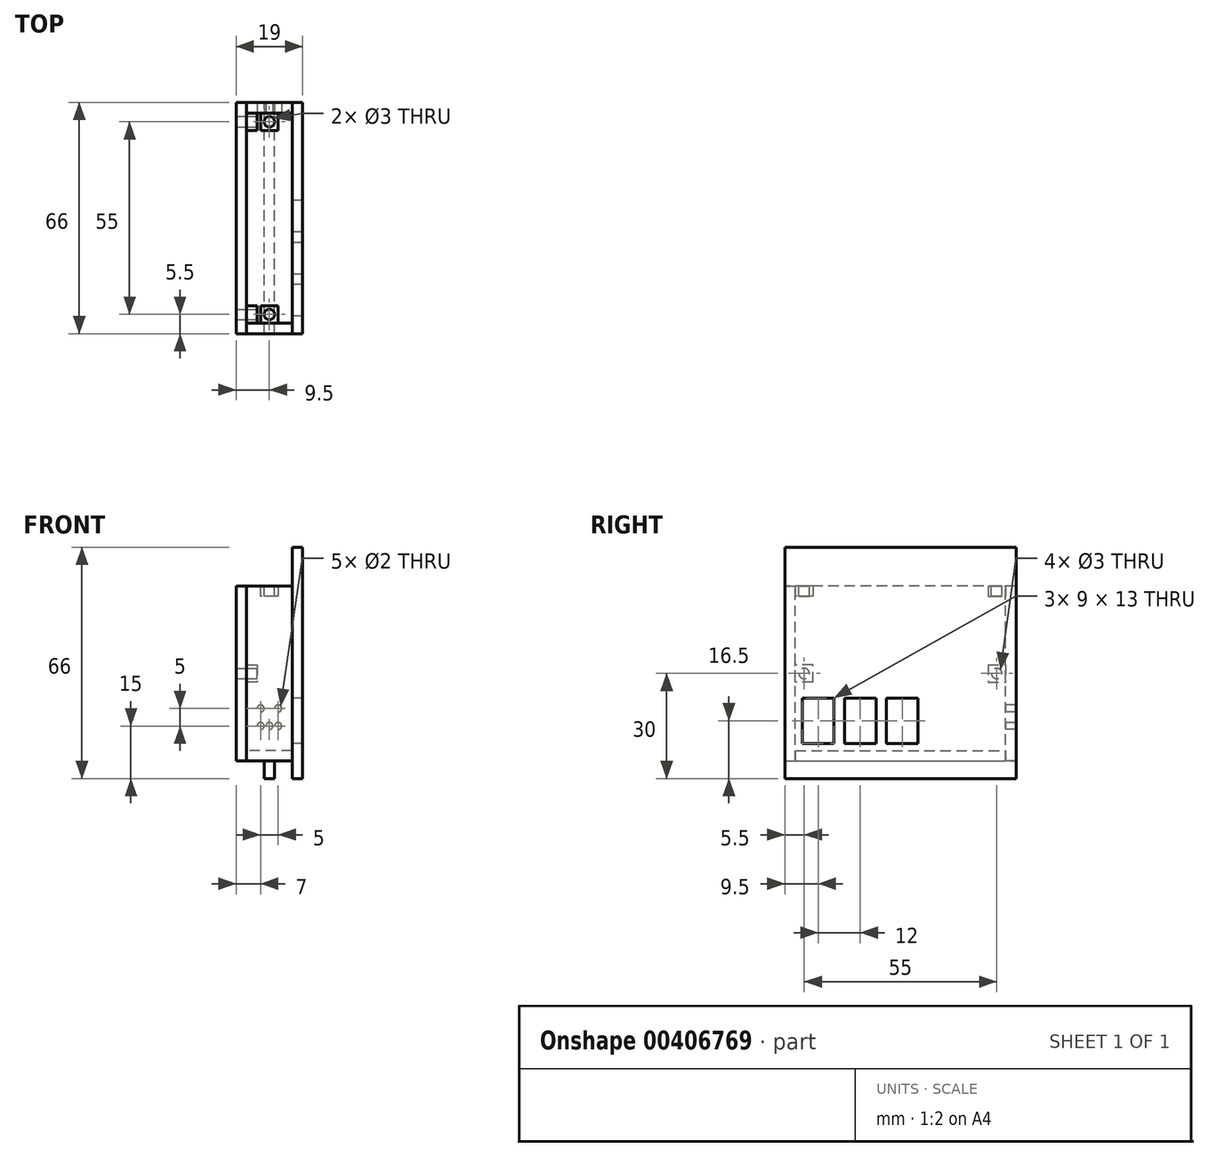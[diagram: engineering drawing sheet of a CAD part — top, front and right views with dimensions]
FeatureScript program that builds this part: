
annotation { "Feature Type Name" : "Feature", "Feature Type Description" : "" }
export const myFeature = defineFeature(function(context is Context, id is Id, definition is map)
    precondition{}
    {
        {
            var Q0;
            Q0=qCreatedBy(makeId("Top.planeOp"),FACE);
            var sketch = newSketch(context, id + "F0", { "sketchPlane" : qUnion([Q0])});
            skLineSegment(sketch, "E0.bottom", {"start": v(6.5, -30) * mm, "end": v(-6.5, -30) * mm});
            skLineSegment(sketch, "E0.top", {"start": v(6.5, 30) * mm, "end": v(-6.5, 30) * mm});
            skLineSegment(sketch, "E0.left", {"start": v(6.5, -30) * mm, "end": v(6.5, 30) * mm});
            skLineSegment(sketch, "E0.right", {"start": v(-6.5, -30) * mm, "end": v(-6.5, 30) * mm});
            skPoint(sketch, "E0.middle", {"position": v(0, 0) * mm});
            skSolve(sketch);
        }
        {
            var Q0;
            Q0=makeQuery(id+"F0.imprint","IMPRINT",FACE,{"disambiguationData":[TD([[makeQuery(id+"F0.imprint","IMPRINT",EDGE,{"derivedFrom":sQuery(id+"F0.wireOp",EDGE,"E0.bottom")}),-1.0]])]});
            extrude(context, id + "F1", {"entities" : qUnion([Q0]), "depth" : 3 * mm});
        }
        {
            var Q0;
            Q0=makeQuery(id+"F1.opExtrude","SWEPT_FACE",FACE,{"disambiguationData":[OSD([sQuery(id+"F0.wireOp",EDGE,"E0.top")])]});
            var sketch = newSketch(context, id + "F2", { "sketchPlane" : qUnion([Q0])});
            skLineSegment(sketch, "E1", {"start": v(-6.5, 0) * mm, "end": v(-6.5, 50) * mm});
            skLineSegment(sketch, "E2", {"start": v(-6.5, 50) * mm, "end": v(6.5, 50) * mm});
            skLineSegment(sketch, "E3", {"start": v(6.5, 50) * mm, "end": v(6.5, 0) * mm});
            skLineSegment(sketch, "E4", {"start": v(-6.5, 10) * mm, "end": v(6.5, 10) * mm, "construction": true});
            skLineSegment(sketch, "E5", {"start": v(-6.5, 12.5) * mm, "end": v(6.5, 12.5) * mm, "construction": true});
            skLineSegment(sketch, "E6", {"start": v(-6.5, 15) * mm, "end": v(6.5, 15) * mm, "construction": true});
            skLineSegment(sketch, "E7", {"start": v(0, 15) * mm, "end": v(0, 10) * mm, "construction": true});
            skLineSegment(sketch, "E8", {"start": v(2.5, 15) * mm, "end": v(2.5, 10) * mm, "construction": true});
            skLineSegment(sketch, "E9", {"start": v(-2.5, 15) * mm, "end": v(-2.5, 10) * mm, "construction": true});
            skCircle(sketch, "E10", {"center": v(-2.5, 15) * mm, "radius": 1 * mm});
            skCircle(sketch, "E11", {"center": v(2.5, 15) * mm, "radius": 1 * mm});
            skCircle(sketch, "E12", {"center": v(2.5, 10) * mm, "radius": 1 * mm});
            skCircle(sketch, "E13", {"center": v(0, 10) * mm, "radius": 1 * mm});
            skCircle(sketch, "E14", {"center": v(-2.5, 10) * mm, "radius": 1 * mm});
            skSolve(sketch);
        }
        {
            var Q0;
            {var subQ2=sQuery(id+"F2.wireOp",EDGE,"E2");Q0=makeQuery(id+"F2.imprint","IMPRINT",FACE,{"disambiguationData":[TD([[makeQuery(id+"F2.imprint","IMPRINT",EDGE,{"derivedFrom":subQ2}),-1.0]])]});}
            var Q1;
            {var subQ1=sQuery(id+"F0.wireOp",EDGE,"E0.top");var subQ2=makeQuery(id+"F1.opExtrude","CAP_EDGE",EDGE,{"disambiguationData":[OSD([subQ1])],"isStart":true});Q1=makeQuery(id+"F2.imprint","IMPRINT",FACE,{"disambiguationData":[TD([[makeQuery(id+"F2.imprint","IMPRINT",EDGE,{"derivedFrom":subQ2}),1.0]])]});}
            extrude(context, id + "F3", {"entities" : qUnion([Q0, Q1]), "depth" : 3 * mm});
        }
        {
            var Q0;
            Q0=makeQuery(id+"F1.opExtrude","SWEPT_FACE",FACE,{"disambiguationData":[OSD([sQuery(id+"F0.wireOp",EDGE,"E0.bottom")])]});
            var sketch = newSketch(context, id + "F4", { "sketchPlane" : qUnion([Q0])});
            skLineSegment(sketch, "E15", {"start": v(-6.5, 0) * mm, "end": v(-6.5, 50) * mm});
            skLineSegment(sketch, "E16", {"start": v(-6.5, 50) * mm, "end": v(6.5, 50) * mm});
            skLineSegment(sketch, "E17", {"start": v(6.5, 50) * mm, "end": v(6.5, 0) * mm});
            skSolve(sketch);
        }
        {
            var Q0;
            {var subQ2=sQuery(id+"F4.wireOp",EDGE,"E16");Q0=makeQuery(id+"F4.imprint","IMPRINT",FACE,{"disambiguationData":[TD([[makeQuery(id+"F4.imprint","IMPRINT",EDGE,{"derivedFrom":subQ2}),-1.0]])]});}
            var Q1;
            {var subQ1=sQuery(id+"F0.wireOp",EDGE,"E0.bottom");var subQ2=makeQuery(id+"F1.opExtrude","CAP_EDGE",EDGE,{"disambiguationData":[OSD([subQ1])],"isStart":true});Q1=makeQuery(id+"F4.imprint","IMPRINT",FACE,{"disambiguationData":[TD([[makeQuery(id+"F4.imprint","IMPRINT",EDGE,{"derivedFrom":subQ2}),-1.0]])]});}
            extrude(context, id + "F5", {"entities" : qUnion([Q0, Q1]), "depth" : 3 * mm});
        }
        {
            var Q0;
            Q0=makeQuery(id+"F1.opExtrude","SWEPT_FACE",FACE,{"disambiguationData":[OSD([sQuery(id+"F0.wireOp",EDGE,"E0.left")])]});
            var sketch = newSketch(context, id + "F6", { "sketchPlane" : qUnion([Q0])});
            skLineSegment(sketch, "E18.bottom", {"start": v(-33, 61) * mm, "end": v(33, 61) * mm});
            skLineSegment(sketch, "E18.top", {"start": v(-33, -5) * mm, "end": v(33, -5) * mm});
            skLineSegment(sketch, "E18.left", {"start": v(-33, 61) * mm, "end": v(-33, -5) * mm});
            skLineSegment(sketch, "E18.right", {"start": v(33, 61) * mm, "end": v(33, -5) * mm});
            skLineSegment(sketch, "E19", {"start": v(-33, 5) * mm, "end": v(33, 5) * mm, "construction": true});
            skLineSegment(sketch, "E20", {"start": v(-33, 18) * mm, "end": v(33, 18) * mm, "construction": true});
            skLineSegment(sketch, "E21.bottom", {"start": v(-28, 18) * mm, "end": v(-19, 18) * mm});
            skLineSegment(sketch, "E21.top", {"start": v(-28, 5) * mm, "end": v(-19, 5) * mm});
            skLineSegment(sketch, "E21.left", {"start": v(-28, 18) * mm, "end": v(-28, 5) * mm});
            skLineSegment(sketch, "E21.right", {"start": v(-19, 18) * mm, "end": v(-19, 5) * mm});
            skLineSegment(sketch, "E22.bottom", {"start": v(-16, 18) * mm, "end": v(-7, 18) * mm});
            skLineSegment(sketch, "E22.top", {"start": v(-16, 5) * mm, "end": v(-7, 5) * mm});
            skLineSegment(sketch, "E22.left", {"start": v(-16, 18) * mm, "end": v(-16, 5) * mm});
            skLineSegment(sketch, "E22.right", {"start": v(-7, 18) * mm, "end": v(-7, 5) * mm});
            skLineSegment(sketch, "E23.bottom", {"start": v(-4, 18) * mm, "end": v(5, 18) * mm});
            skLineSegment(sketch, "E23.top", {"start": v(-4, 5) * mm, "end": v(5, 5) * mm});
            skLineSegment(sketch, "E23.left", {"start": v(-4, 18) * mm, "end": v(-4, 5) * mm});
            skLineSegment(sketch, "E23.right", {"start": v(5, 18) * mm, "end": v(5, 5) * mm});
            skSolve(sketch);
        }
        {
            var Q0;
            Q0=makeQuery(id+"F6.imprint","IMPRINT",FACE,{"disambiguationData":[TD([[makeQuery(id+"F6.imprint","IMPRINT",EDGE,{"derivedFrom":sQuery(id+"F6.wireOp",EDGE,"E18.bottom")}),-1.0]])]});
            var Q1;
            {var subQ0=sQuery(id+"F0.wireOp",EDGE,"E0.left");Q1=makeQuery(id+"F6.imprint","IMPRINT",FACE,{"disambiguationData":[TD([[makeQuery(id+"F6.imprint","IMPRINT",EDGE,{"derivedFrom":makeQuery(id+"F1.opExtrude","CAP_EDGE",EDGE,{"disambiguationData":[OSD([subQ0])],"isStart":true})}),1.0]])]});}
            extrude(context, id + "F7", {"entities" : qUnion([Q0, Q1]), "depth" : 3 * mm});
        }
        {
            var Q0;
            Q0=makeQuery(id+"F1.opExtrude","SWEPT_FACE",FACE,{"disambiguationData":[OSD([sQuery(id+"F0.wireOp",EDGE,"E0.right")])]});
            var sketch = newSketch(context, id + "F8", { "sketchPlane" : qUnion([Q0])});
            skLineSegment(sketch, "E24", {"start": v(-30, 0) * mm, "end": v(-33, 0) * mm});
            skLineSegment(sketch, "E25", {"start": v(-33, 0) * mm, "end": v(-33, 50) * mm});
            skLineSegment(sketch, "E26", {"start": v(-33, 50) * mm, "end": v(33, 50) * mm});
            skLineSegment(sketch, "E27", {"start": v(33, 50) * mm, "end": v(33, 0) * mm});
            skLineSegment(sketch, "E28", {"start": v(33, 0) * mm, "end": v(30, 0) * mm});
            skLineSegment(sketch, "E29", {"start": v(-33, 25) * mm, "end": v(33, 25) * mm, "construction": true});
            skLineSegment(sketch, "E30", {"start": v(-27.5, 28.67) * mm, "end": v(-27.5, 21.1) * mm, "construction": true});
            skLineSegment(sketch, "E31", {"start": v(27.5, 28.93) * mm, "end": v(27.5, 20.46) * mm, "construction": true});
            skCircle(sketch, "E32", {"center": v(-27.5, 25) * mm, "radius": 1.5 * mm});
            skCircle(sketch, "E33", {"center": v(27.5, 25) * mm, "radius": 1.5 * mm});
            skSolve(sketch);
        }
        {
            var Q0;
            Q0=makeQuery(id+"F8.imprint","IMPRINT",FACE,{"disambiguationData":[TD([[makeQuery(id+"F8.imprint","IMPRINT",EDGE,{"derivedFrom":sQuery(id+"F8.wireOp",EDGE,"E24")}),-1.0]])]});
            var Q1;
            {var subQ0=sQuery(id+"F0.wireOp",EDGE,"E0.right");Q1=makeQuery(id+"F8.imprint","IMPRINT",FACE,{"disambiguationData":[TD([[makeQuery(id+"F8.imprint","IMPRINT",EDGE,{"derivedFrom":makeQuery(id+"F1.opExtrude","CAP_EDGE",EDGE,{"disambiguationData":[OSD([subQ0])],"isStart":true})}),-1.0]])]});}
            extrude(context, id + "F9", {"entities" : qUnion([Q0, Q1]), "depth" : 3 * mm});
        }
        {
            var Q0;
            Q0=makeQuery(id+"F1.opExtrude","CAP_FACE",FACE,{"disambiguationData":[OSD([sQuery(id+"F0.wireOp",EDGE,"E0.bottom"),sQuery(id+"F0.wireOp",EDGE,"E0.top"),sQuery(id+"F0.wireOp",EDGE,"E0.left"),sQuery(id+"F0.wireOp",EDGE,"E0.right")])],"isStart":true});
            var sketch = newSketch(context, id + "F10", { "sketchPlane" : qUnion([Q0])});
            skLineSegment(sketch, "E34.bottom", {"start": v(-1.5, 33) * mm, "end": v(1.5, 33) * mm});
            skLineSegment(sketch, "E34.top", {"start": v(-1.5, -33) * mm, "end": v(1.5, -33) * mm});
            skLineSegment(sketch, "E34.left", {"start": v(-1.5, 33) * mm, "end": v(-1.5, -33) * mm});
            skLineSegment(sketch, "E34.right", {"start": v(1.5, 33) * mm, "end": v(1.5, -33) * mm});
            skSolve(sketch);
        }
        {
            var Q0;
            {var subQ0=sQuery(id+"F10.wireOp",EDGE,"E34.left");var subQ1=makeQuery(id+"F1.opExtrude","CAP_EDGE",EDGE,{"disambiguationData":[OSD([sQuery(id+"F0.wireOp",EDGE,"E0.bottom")])],"isStart":true});var subQ2=makeQuery(id+"F10.imprint","INTERSECT",VERTEX,{"derivedFrom":[subQ1,subQ0]});Q0=makeQuery(id+"F10.imprint","IMPRINT",FACE,{"disambiguationData":[TD([[makeQuery(id+"F10.imprint","IMPRINT",EDGE,{"disambiguationData":[TD([[subQ2,-1.0]])],"derivedFrom":subQ0}),1.0]])]});}
            var Q1;
            {var subQ0=sQuery(id+"F10.wireOp",EDGE,"E34.top");Q1=makeQuery(id+"F10.imprint","IMPRINT",FACE,{"disambiguationData":[TD([[makeQuery(id+"F10.imprint","IMPRINT",EDGE,{"derivedFrom":subQ0}),1.0]])]});}
            var Q2;
            {var subQ0=sQuery(id+"F10.wireOp",EDGE,"E34.bottom");Q2=makeQuery(id+"F10.imprint","IMPRINT",FACE,{"disambiguationData":[TD([[makeQuery(id+"F10.imprint","IMPRINT",EDGE,{"derivedFrom":subQ0}),-1.0]])]});}
            extrude(context, id + "F11", {"entities" : qUnion([Q0, Q1, Q2]), "depth" : 5 * mm});
        }
        {
            var Q0;
            Q0=makeQuery(id+"F3.opExtrude","CAP_FACE",FACE,{"disambiguationData":[OSD([sQuery(id+"F0.wireOp",EDGE,"E0.top"),sQuery(id+"F2.wireOp",EDGE,"E1"),sQuery(id+"F2.wireOp",EDGE,"E2"),sQuery(id+"F2.wireOp",EDGE,"E3"),sQuery(id+"F2.wireOp",EDGE,"E10"),sQuery(id+"F2.wireOp",EDGE,"E11"),sQuery(id+"F2.wireOp",EDGE,"E12"),sQuery(id+"F2.wireOp",EDGE,"E13"),sQuery(id+"F2.wireOp",EDGE,"E14")])],"isStart":true});
            var sketch = newSketch(context, id + "F12", { "sketchPlane" : qUnion([Q0])});
            skLineSegment(sketch, "E35", {"start": v(-2.5, 50) * mm, "end": v(-2.5, 47) * mm});
            skLineSegment(sketch, "E36", {"start": v(-2.5, 47) * mm, "end": v(2.5, 47) * mm});
            skLineSegment(sketch, "E37", {"start": v(2.5, 47) * mm, "end": v(2.5, 50) * mm});
            skLineSegment(sketch, "E38", {"start": v(0, 50) * mm, "end": v(0, 45.23) * mm, "construction": true});
            skPoint(sketch, "E38.endSnap0", {"position": v(0, 50) * mm});
            skLineSegment(sketch, "E39", {"start": v(-6.5, 25) * mm, "end": v(6.5, 25) * mm, "construction": true});
            skLineSegment(sketch, "E40", {"start": v(-6.5, 27.5) * mm, "end": v(-3.5, 27.5) * mm});
            skLineSegment(sketch, "E41", {"start": v(-3.5, 27.5) * mm, "end": v(-3.5, 22.5) * mm});
            skLineSegment(sketch, "E42", {"start": v(-3.5, 22.5) * mm, "end": v(-6.5, 22.5) * mm});
            skSolve(sketch);
        }
        {
            var Q0;
            {var subQ0=sQuery(id+"F12.wireOp",EDGE,"E35");Q0=makeQuery(id+"F12.imprint","IMPRINT",FACE,{"disambiguationData":[TD([[makeQuery(id+"F12.imprint","IMPRINT",EDGE,{"derivedFrom":subQ0}),1.0]])]});}
            var Q1;
            {var subQ0=sQuery(id+"F12.wireOp",EDGE,"E40");Q1=makeQuery(id+"F12.imprint","IMPRINT",FACE,{"disambiguationData":[TD([[makeQuery(id+"F12.imprint","IMPRINT",EDGE,{"derivedFrom":subQ0}),-1.0]])]});}
            extrude(context, id + "F13", {"entities" : qUnion([Q0, Q1]), "depth" : 5 * mm});
        }
        {
            var Q0;
            Q0=makeQuery(id+"F13.opExtrude","SWEPT_FACE",FACE,{"disambiguationData":[OSD([sQuery(id+"F12.wireOp",EDGE,"E41")])]});
            var sketch = newSketch(context, id + "F14", { "sketchPlane" : qUnion([Q0])});
            skCircle(sketch, "E43", {"center": v(27.5, 25) * mm, "radius": 1.5 * mm});
            skPoint(sketch, "E43.centerSnap0", {"position": v(25, 25) * mm});
            skPoint(sketch, "E43.centerSnap1", {"position": v(27.5, 27.5) * mm});
            skSolve(sketch);
        }
        {
            var Q0;
            Q0=makeQuery(id+"F14.imprint","IMPRINT",FACE,{"disambiguationData":[TD([[makeQuery(id+"F14.imprint","IMPRINT",EDGE,{"derivedFrom":sQuery(id+"F14.wireOp",EDGE,"E43")}),1.0]])]});
            extrude(context, id + "F15", {"entities" : qUnion([Q0]), "operationType" : NewBodyOperationType.REMOVE, "oppositeDirection" : true, "depth" : 3 * mm});
        }
        {
            var Q0;
            Q0=makeQuery(id+"F13.opExtrude","SWEPT_FACE",FACE,{"disambiguationData":[OSD([sQuery(id+"F2.wireOp",EDGE,"E2")])]});
            var sketch = newSketch(context, id + "F16", { "sketchPlane" : qUnion([Q0])});
            skCircle(sketch, "E44", {"center": v(0, 27.5) * mm, "radius": 1.5 * mm});
            skPoint(sketch, "E44.centerSnap0", {"position": v(2.5, 27.5) * mm});
            skSolve(sketch);
        }
        {
            var Q0;
            Q0=makeQuery(id+"F16.imprint","IMPRINT",FACE,{"disambiguationData":[TD([[makeQuery(id+"F16.imprint","IMPRINT",EDGE,{"derivedFrom":sQuery(id+"F16.wireOp",EDGE,"E44")}),1.0]])]});
            extrude(context, id + "F17", {"entities" : qUnion([Q0]), "operationType" : NewBodyOperationType.REMOVE, "oppositeDirection" : true, "depth" : 3 * mm});
        }
        {
            var Q0;
            Q0=makeQuery(id+"F5.opExtrude","CAP_FACE",FACE,{"disambiguationData":[OSD([sQuery(id+"F0.wireOp",EDGE,"E0.bottom"),sQuery(id+"F4.wireOp",EDGE,"E15"),sQuery(id+"F4.wireOp",EDGE,"E16"),sQuery(id+"F4.wireOp",EDGE,"E17")])],"isStart":true});
            var sketch = newSketch(context, id + "F18", { "sketchPlane" : qUnion([Q0])});
            skLineSegment(sketch, "E45", {"start": v(6.5, 25) * mm, "end": v(-6.5, 25) * mm, "construction": true});
            skLineSegment(sketch, "E46", {"start": v(0, 50) * mm, "end": v(0, 43.73) * mm, "construction": true});
            skPoint(sketch, "E46.endSnap0", {"position": v(0, 50) * mm});
            skLineSegment(sketch, "E47", {"start": v(-2.5, 50) * mm, "end": v(-2.5, 47) * mm});
            skLineSegment(sketch, "E48", {"start": v(-2.5, 47) * mm, "end": v(2.5, 47) * mm});
            skLineSegment(sketch, "E49", {"start": v(2.5, 47) * mm, "end": v(2.5, 50) * mm});
            skLineSegment(sketch, "E50", {"start": v(6.5, 27.5) * mm, "end": v(3.5, 27.5) * mm});
            skLineSegment(sketch, "E51", {"start": v(3.5, 27.5) * mm, "end": v(3.5, 22.5) * mm});
            skLineSegment(sketch, "E52", {"start": v(3.5, 22.5) * mm, "end": v(6.5, 22.5) * mm});
            skSolve(sketch);
        }
        {
            var Q0;
            {var subQ0=sQuery(id+"F18.wireOp",EDGE,"E50");Q0=makeQuery(id+"F18.imprint","IMPRINT",FACE,{"disambiguationData":[TD([[makeQuery(id+"F18.imprint","IMPRINT",EDGE,{"derivedFrom":subQ0}),1.0]])]});}
            var Q1;
            {var subQ0=sQuery(id+"F18.wireOp",EDGE,"E47");Q1=makeQuery(id+"F18.imprint","IMPRINT",FACE,{"disambiguationData":[TD([[makeQuery(id+"F18.imprint","IMPRINT",EDGE,{"derivedFrom":subQ0}),1.0]])]});}
            extrude(context, id + "F19", {"entities" : qUnion([Q0, Q1]), "depth" : 5 * mm});
        }
        {
            var Q0;
            Q0=makeQuery(id+"F19.opExtrude","SWEPT_FACE",FACE,{"disambiguationData":[OSD([sQuery(id+"F4.wireOp",EDGE,"E16")])]});
            var sketch = newSketch(context, id + "F20", { "sketchPlane" : qUnion([Q0])});
            skCircle(sketch, "E53", {"center": v(0, -27.5) * mm, "radius": 1.5 * mm});
            skPoint(sketch, "E53.centerSnap0", {"position": v(2.5, -27.5) * mm});
            skSolve(sketch);
        }
        {
            var Q0;
            Q0=makeQuery(id+"F20.imprint","IMPRINT",FACE,{"disambiguationData":[TD([[makeQuery(id+"F20.imprint","IMPRINT",EDGE,{"derivedFrom":sQuery(id+"F20.wireOp",EDGE,"E53")}),1.0]])]});
            extrude(context, id + "F21", {"entities" : qUnion([Q0]), "operationType" : NewBodyOperationType.REMOVE, "oppositeDirection" : true, "depth" : 3 * mm});
        }
        {
            var Q0;
            Q0=makeQuery(id+"F19.opExtrude","SWEPT_FACE",FACE,{"disambiguationData":[OSD([sQuery(id+"F18.wireOp",EDGE,"E51")])]});
            var sketch = newSketch(context, id + "F22", { "sketchPlane" : qUnion([Q0])});
            skCircle(sketch, "E54", {"center": v(-27.5, 25) * mm, "radius": 1.5 * mm});
            skPoint(sketch, "E54.centerSnap0", {"position": v(-27.5, 27.5) * mm});
            skPoint(sketch, "E54.centerSnap1", {"position": v(-30, 25) * mm});
            skSolve(sketch);
        }
        {
            var Q0;
            Q0=makeQuery(id+"F22.imprint","IMPRINT",FACE,{"disambiguationData":[TD([[makeQuery(id+"F22.imprint","IMPRINT",EDGE,{"derivedFrom":sQuery(id+"F22.wireOp",EDGE,"E54")}),1.0]])]});
            extrude(context, id + "F23", {"entities" : qUnion([Q0]), "operationType" : NewBodyOperationType.REMOVE, "oppositeDirection" : true, "depth" : 3 * mm});
        }
    });
